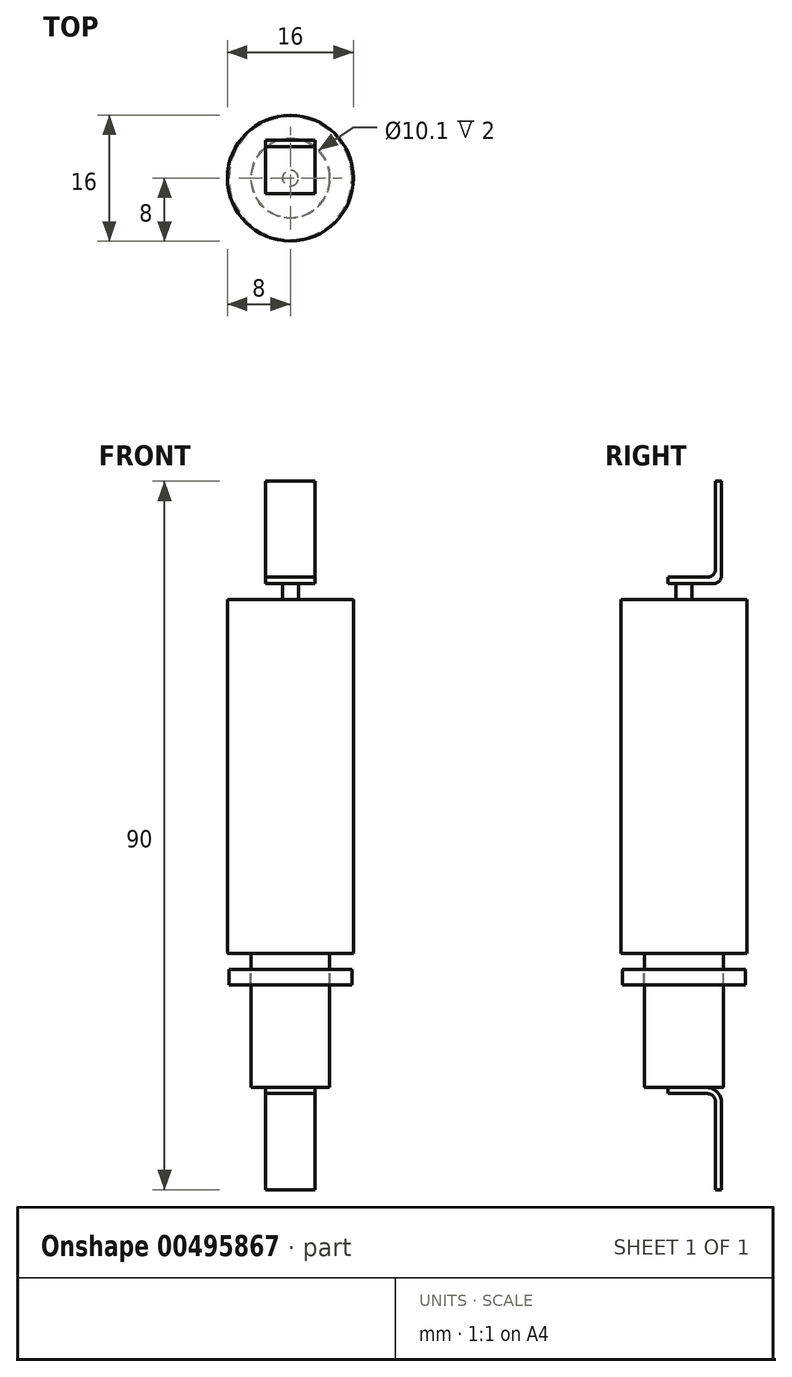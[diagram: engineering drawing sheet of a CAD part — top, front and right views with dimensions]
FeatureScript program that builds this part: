
annotation { "Feature Type Name" : "Feature", "Feature Type Description" : "" }
export const myFeature = defineFeature(function(context is Context, id is Id, definition is map)
    precondition{}
    {
        {
            var Q0;
            Q0=qCreatedBy(makeId("Top.planeOp"),FACE);
            var sketch = newSketch(context, id + "F0", { "sketchPlane" : qUnion([Q0])});
            skCircle(sketch, "E0", {"center": v(0, 0) * mm, "radius": 8 * mm});
            skSolve(sketch);
        }
        {
            var Q0;
            Q0=qSketchRegion(id+"F0",true);
            extrude(context, id + "F1", {"entities" : qUnion([Q0]), "depth" : 45 * mm});
        }
        {
            var Q0;
            Q0=makeQuery(id+"F1.opExtrude","CAP_FACE",FACE,{"disambiguationData":[OSD([sQuery(id+"F0.wireOp",EDGE,"E0")])],"isStart":true});
            var sketch = newSketch(context, id + "F2", { "sketchPlane" : qUnion([Q0])});
            skCircle(sketch, "E1", {"center": v(0, 0) * mm, "radius": 5 * mm});
            skSolve(sketch);
        }
        {
            var Q0;
            Q0=qSketchRegion(id+"F2",true);
            extrude(context, id + "F3", {"entities" : qUnion([Q0]), "operationType" : NewBodyOperationType.ADD, "depth" : 17 * mm});
        }
        {
            var Q0;
            Q0=makeQuery(id+"F1.opExtrude","CAP_FACE",FACE,{"disambiguationData":[OSD([sQuery(id+"F0.wireOp",EDGE,"E0")])],"isStart":true});
            var sketch = newSketch(context, id + "F4", { "sketchPlane" : qUnion([Q0])});
            skCircle(sketch, "E2", {"center": v(0, 0) * mm, "radius": 5.05 * mm});
            skCircle(sketch, "E3", {"center": v(0, 0) * mm, "radius": 7.8 * mm});
            skSolve(sketch);
        }
        {
            var Q0;
            Q0=qSketchRegion(id+"F4",true);
            extrude(context, id + "F5", {"entities" : qUnion([Q0]), "depth" : 4 * mm, "hasSecondDirection" : true, "secondDirectionOppositeDirection" : false, "secondDirectionDepth" : 2 * mm});
        }
        {
            var Q0;
            Q0=makeQuery(id+"F1.opExtrude","CAP_FACE",FACE,{"disambiguationData":[OSD([sQuery(id+"F0.wireOp",EDGE,"E0")])],"isStart":false});
            var sketch = newSketch(context, id + "F6", { "sketchPlane" : qUnion([Q0])});
            skCircle(sketch, "E4", {"center": v(0, 0) * mm, "radius": 1 * mm});
            skSolve(sketch);
        }
        {
            var Q0;
            Q0=qSketchRegion(id+"F6",true);
            extrude(context, id + "F7", {"entities" : qUnion([Q0]), "operationType" : NewBodyOperationType.ADD, "depth" : 2 * mm});
        }
        {
            var Q0;
            Q0=qCreatedBy(makeId("Right.planeOp"),FACE);
            var sketch = newSketch(context, id + "F8", { "sketchPlane" : qUnion([Q0])});
            skLineSegment(sketch, "E5", {"start": v(0, 47) * mm, "end": v(3.8, 47) * mm});
            skLineSegment(sketch, "E6", {"start": v(4.8, 48) * mm, "end": v(4.8, 60) * mm});
            skLineSegment(sketch, "E7", {"start": v(4.8, 60) * mm, "end": v(4, 60) * mm});
            skLineSegment(sketch, "E8", {"start": v(4, 60) * mm, "end": v(4, 48.8) * mm});
            skLineSegment(sketch, "E9", {"start": v(3, 47.8) * mm, "end": v(-2, 47.8) * mm});
            skLineSegment(sketch, "E10", {"start": v(-2, 47.8) * mm, "end": v(-2, 47) * mm});
            skLineSegment(sketch, "E11", {"start": v(-2, 47) * mm, "end": v(0, 47) * mm});
            skPoint(sketch, "E12.visualSharp", {"position": v(4, 47.8) * mm});
            skArc(sketch, "E12.filletArc", {"start": v(3, 47.8) * mm, "mid": v(3.7, 48.1) * mm, "end": v(4, 48.8) * mm});
            skPoint(sketch, "E13.visualSharp", {"position": v(4.8, 47) * mm});
            skArc(sketch, "E13.filletArc", {"start": v(3.8, 47) * mm, "mid": v(4.5, 47.3) * mm, "end": v(4.8, 48) * mm});
            skLineSegment(sketch, "E14", {"start": v(-2, -17) * mm, "end": v(-2, -17.8) * mm});
            skLineSegment(sketch, "E15", {"start": v(-2, -17.8) * mm, "end": v(3, -17.8) * mm});
            skLineSegment(sketch, "E16", {"start": v(4, -18.8) * mm, "end": v(4, -30) * mm});
            skLineSegment(sketch, "E17", {"start": v(4, -30) * mm, "end": v(4.8, -30) * mm});
            skLineSegment(sketch, "E18", {"start": v(4.8, -30) * mm, "end": v(4.8, -19) * mm});
            skLineSegment(sketch, "E19", {"start": v(2.8, -17) * mm, "end": v(-2, -17) * mm});
            skPoint(sketch, "E20.visualSharp", {"position": v(4, -17.8) * mm});
            skArc(sketch, "E20.filletArc", {"start": v(4, -18.8) * mm, "mid": v(3.7, -18.1) * mm, "end": v(3, -17.8) * mm});
            skPoint(sketch, "E21.visualSharp", {"position": v(4.8, -17) * mm});
            skArc(sketch, "E21.filletArc", {"start": v(4.8, -19) * mm, "mid": v(4.21, -17.59) * mm, "end": v(2.8, -17) * mm});
            skSolve(sketch);
        }
        {
            var Q0;
            Q0=qSketchRegion(id+"F8",true);
            extrude(context, id + "F9", {"entities" : qUnion([Q0]), "endBound" : BoundingType.SYMMETRIC, "depth" : 6.3 * mm});
        }
    });
